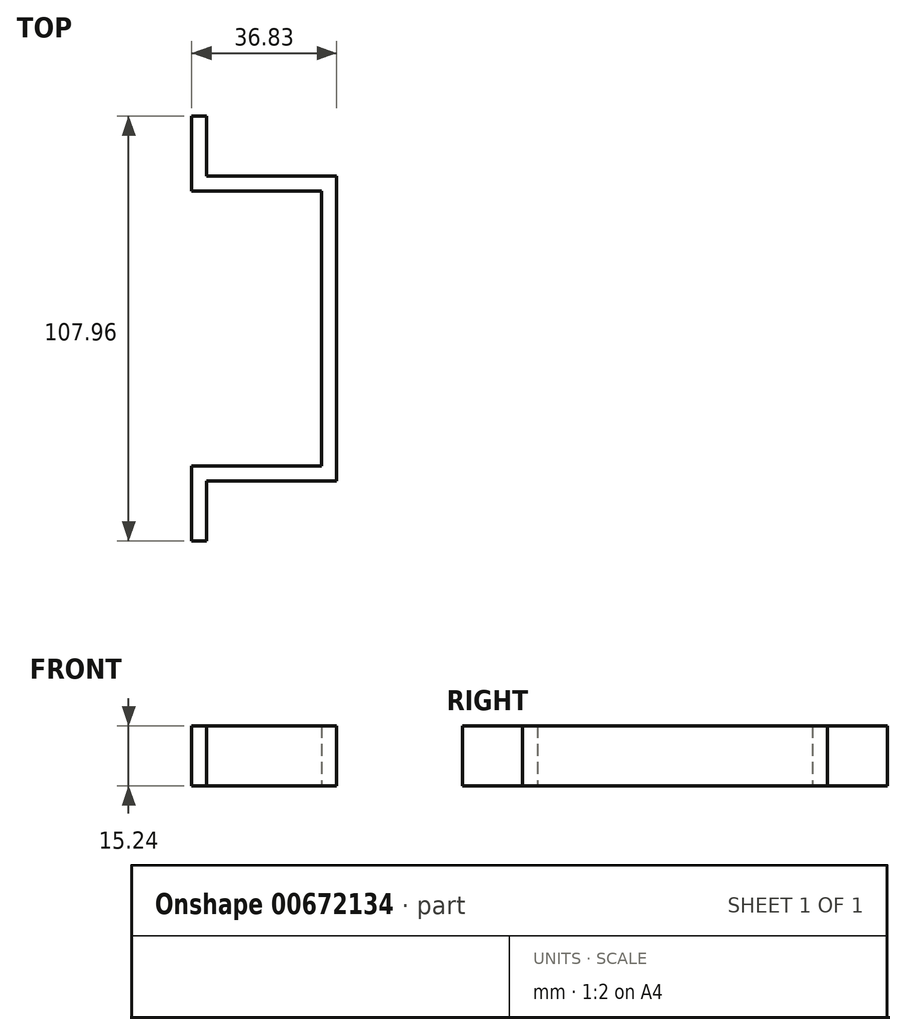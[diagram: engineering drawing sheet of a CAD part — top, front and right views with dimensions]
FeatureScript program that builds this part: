
annotation { "Feature Type Name" : "Feature", "Feature Type Description" : "" }
export const myFeature = defineFeature(function(context is Context, id is Id, definition is map)
    precondition{}
    {
        {
            var Q0;
            Q0=qCreatedBy(makeId("Top.planeOp"),FACE);
            var sketch = newSketch(context, id + "F0", { "sketchPlane" : qUnion([Q0])});
            skLineSegment(sketch, "E0.left", {"start": v(1.9, -34.92) * mm, "end": v(1.9, 34.93) * mm});
            skLineSegment(sketch, "E0.right", {"start": v(-1.9, -34.93) * mm, "end": v(-1.9, 34.93) * mm});
            skPoint(sketch, "E0.middle", {"position": v(0, 0) * mm});
            skLineSegment(sketch, "E1.bottom", {"start": v(-1.9, 34.92) * mm, "end": v(-34.92, 34.92) * mm});
            skLineSegment(sketch, "E1.top", {"start": v(1.9, 38.74) * mm, "end": v(-31.11, 38.73) * mm});
            skLineSegment(sketch, "E1.left", {"start": v(1.9, 34.93) * mm, "end": v(1.9, 38.74) * mm});
            skLineSegment(sketch, "E1.right", {"start": v(-34.92, 34.92) * mm, "end": v(-34.92, 38.73) * mm});
            skLineSegment(sketch, "E2.bottom", {"start": v(-1.9, -34.93) * mm, "end": v(-34.92, -34.93) * mm});
            skLineSegment(sketch, "E2.top", {"start": v(1.9, -38.74) * mm, "end": v(-31.11, -38.74) * mm});
            skLineSegment(sketch, "E2.left", {"start": v(1.9, -34.93) * mm, "end": v(1.9, -38.74) * mm});
            skLineSegment(sketch, "E2.right", {"start": v(-34.92, -34.93) * mm, "end": v(-34.92, -38.74) * mm});
            skLineSegment(sketch, "E3.top", {"start": v(-34.92, 53.98) * mm, "end": v(-31.11, 53.98) * mm});
            skLineSegment(sketch, "E3.left", {"start": v(-34.92, 38.73) * mm, "end": v(-34.92, 53.97) * mm});
            skLineSegment(sketch, "E3.right", {"start": v(-31.11, 38.73) * mm, "end": v(-31.11, 53.97) * mm});
            skLineSegment(sketch, "E4.top", {"start": v(-34.92, -53.98) * mm, "end": v(-31.11, -53.98) * mm});
            skLineSegment(sketch, "E4.left", {"start": v(-34.92, -38.74) * mm, "end": v(-34.92, -53.98) * mm});
            skLineSegment(sketch, "E4.right", {"start": v(-31.11, -38.74) * mm, "end": v(-31.11, -53.98) * mm});
            skSolve(sketch);
        }
        {
            var Q0;
            Q0=makeQuery(id+"F0.imprint","IMPRINT",FACE,{"disambiguationData":[TD([[makeQuery(id+"F0.imprint","IMPRINT",EDGE,{"derivedFrom":sQuery(id+"F0.wireOp",EDGE,"E0.left")}),1.0]])]});
            extrude(context, id + "F1", {"entities" : qUnion([Q0]), "depth" : 15.24 * mm, "offsetDistance" : 25.4 * mm});
        }
    });
